FCSTD DOCUMENT  (FreeCAD 1.0R39109 (Git))
Label: wallspeakers v0.1
License: All rights reserved
LicenseURL: http://en.wikipedia.org/wiki/All_rights_reserved
objects: Sketcher::SketchObject×1, PartDesign::Body×1, Spreadsheet::Sheet×1
note: 3 computed .brp shape members not serialized (recipe doc carries the construction recipe); baked Part::Feature solids carry a one-line shape summary decoded from their .brp

FEATURE [Sketcher::SketchObject] Sketch
  ArcFitTolerance = 1e-06
  AttachmentSupport = -> [XY_Plane]
  FullyConstrained = false
  MakeInternals = false
  MapMode = 5
  sketch-geometry (4):
    g0: LineSegment StartX=0 StartY=0 StartZ=0 EndX=16.4424 EndY=0 EndZ=0
    g1: LineSegment StartX=16.4424 StartY=0 StartZ=0 EndX=16.4424 EndY=31.3561 EndZ=0
    g2: LineSegment StartX=16.4424 StartY=31.3561 StartZ=0 EndX=0 EndY=31.3561 EndZ=0
    g3: LineSegment StartX=0 StartY=31.3561 StartZ=0 EndX=0 EndY=0 EndZ=0
  constraints (9):
    c: Coincident(g0,g1)
    c: Coincident(g1,g2)
    c: Coincident(g2,g3)
    c: Coincident(g3,g0)
    c: Horizontal(g0)
    c: Horizontal(g2)
    c: Vertical(g1)
    c: Vertical(g3)
    c: Coincident(g0,g-1)
FEATURE [PartDesign::Body] Body  label="Backplate"
  AllowCompound = false
  Group = -> [Sketch]
  Origin = -> Origin
FEATURE [Spreadsheet::Sheet] Spreadsheet  label="params"
  cells = A1='width; B1(width)=180; A2='height; B2(height)=500; A3='backplate_thickness; B3(backplate_thickness)=6; A4='frontplate_thickness; B4(frontplate_thickness)=9; A5='wall_thickness; B5(wall_thickness)=5
